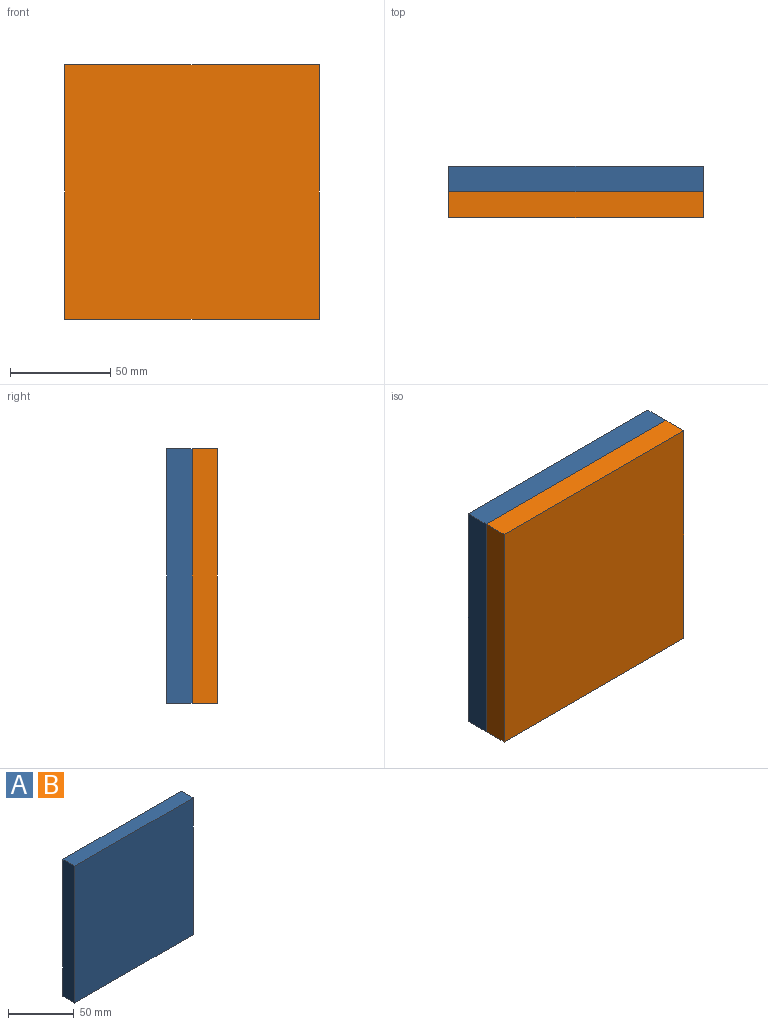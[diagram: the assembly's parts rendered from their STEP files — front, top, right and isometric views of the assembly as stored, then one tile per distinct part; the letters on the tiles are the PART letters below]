
ASSEMBLY  parts=2 mates=1
PART A: 6 faces, bbox 127x12.7x127 mm
  f0: plane 127x12.7mm, normal (0,0,1), area 1612.9mm2, adj f1,f3,f4,f5
  f1: plane 127x12.7mm, normal (-1,0,0), area 1612.9mm2, adj f0,f2,f4,f5
  f2: plane 127x12.7mm, normal (0,0,-1), area 1612.9mm2, adj f1,f3,f4,f5
  f3: plane 127x12.7mm, normal (1,0,0), area 1612.9mm2, adj f0,f2,f4,f5
  f4: plane 127x127mm, normal (0,-1,0), area 16129mm2, adj f0,f1,f2,f3
  f5: plane 127x127mm, normal (0,1,0), area 16129mm2, adj f0,f1,f2,f3
PART B: same geometry as A
PLACE A t=(-101.36,-17.87,14.71)mm
PLACE B t=(-101.36,-30.57,14.71)mm
MATE fastened A.f4 <-> B.f5  axis (0,-1,0) through (-45.47,-30.57,-16)mm
